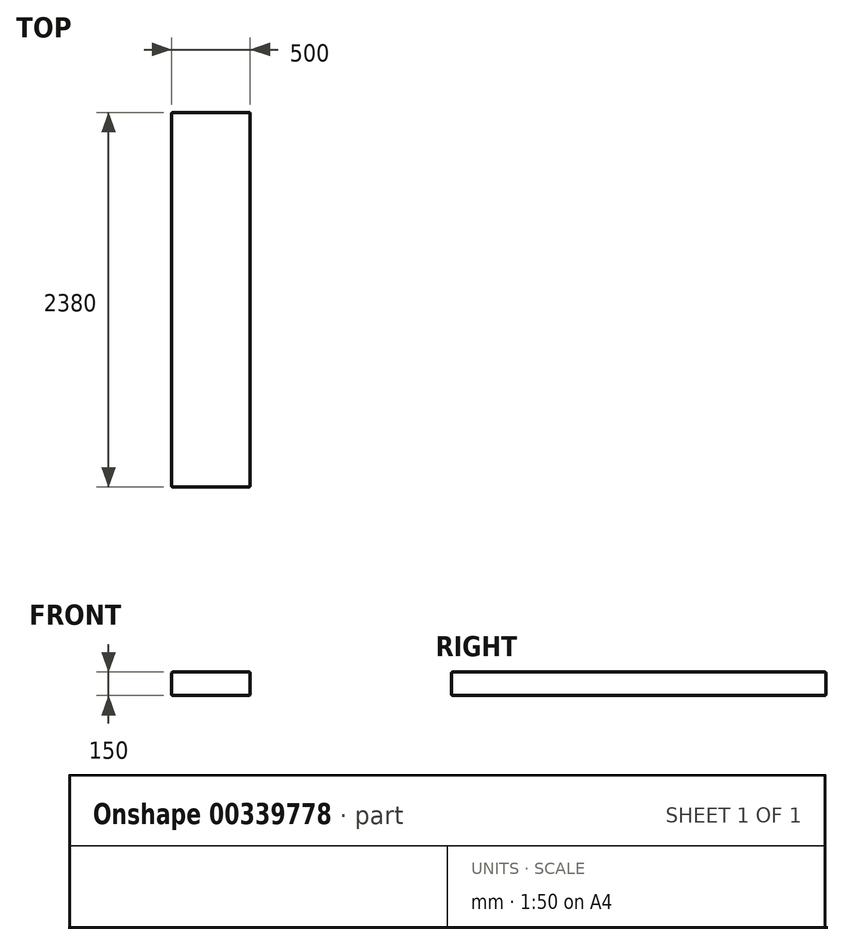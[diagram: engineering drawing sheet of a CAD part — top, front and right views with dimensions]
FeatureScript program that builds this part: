
annotation { "Feature Type Name" : "Feature", "Feature Type Description" : "" }
export const myFeature = defineFeature(function(context is Context, id is Id, definition is map)
    precondition{}
    {
        {
            var Q0;
            Q0=qCreatedBy(makeId("Top.planeOp"),FACE);
            var sketch = newSketch(context, id + "F0", { "sketchPlane" : qUnion([Q0])});
            skLineSegment(sketch, "E0.bottom", {"start": v(0, 0) * mm, "end": v(500, 0) * mm});
            skLineSegment(sketch, "E0.top", {"start": v(0, 2380) * mm, "end": v(500, 2380) * mm});
            skLineSegment(sketch, "E0.left", {"start": v(0, 0) * mm, "end": v(0, 2380) * mm});
            skLineSegment(sketch, "E0.right", {"start": v(500, 0) * mm, "end": v(500, 2380) * mm});
            skSolve(sketch);
        }
        {
            var Q0;
            Q0=makeQuery(id+"F0.imprint","IMPRINT",FACE,{"disambiguationData":[TD([[makeQuery(id+"F0.imprint","IMPRINT",EDGE,{"derivedFrom":sQuery(id+"F0.wireOp",EDGE,"E0.bottom")}),1.0]])]});
            extrude(context, id + "F1", {"entities" : qUnion([Q0]), "depth" : 150 * mm});
        }
        {
            var Q0;
            Q0=makeQuery(id+"F1.opExtrude","CAP_FACE",FACE,{"disambiguationData":[OSD([sQuery(id+"F0.wireOp",EDGE,"E0.bottom"),sQuery(id+"F0.wireOp",EDGE,"E0.top"),sQuery(id+"F0.wireOp",EDGE,"E0.left"),sQuery(id+"F0.wireOp",EDGE,"E0.right")])],"isStart":false});
            var Q1;
            Q1=makeQuery(id+"F1.opExtrude","SWEPT_FACE",FACE,{"disambiguationData":[OSD([sQuery(id+"F0.wireOp",EDGE,"E0.right")])]});
            var Q2;
            Q2=makeQuery(id+"F1.opExtrude","SWEPT_FACE",FACE,{"disambiguationData":[OSD([sQuery(id+"F0.wireOp",EDGE,"E0.bottom")])]});
            var Q3;
            Q3=makeQuery(id+"F1.opExtrude","SWEPT_FACE",FACE,{"disambiguationData":[OSD([sQuery(id+"F0.wireOp",EDGE,"E0.left")])]});
            var Q4;
            Q4=makeQuery(id+"F1.opExtrude","SWEPT_FACE",FACE,{"disambiguationData":[OSD([sQuery(id+"F0.wireOp",EDGE,"E0.top")])]});
            var Q5;
            Q5=makeQuery(id+"F1.opExtrude","CAP_FACE",FACE,{"disambiguationData":[OSD([sQuery(id+"F0.wireOp",EDGE,"E0.bottom"),sQuery(id+"F0.wireOp",EDGE,"E0.top"),sQuery(id+"F0.wireOp",EDGE,"E0.left"),sQuery(id+"F0.wireOp",EDGE,"E0.right")])],"isStart":true});
            fillet(context, id + "F2", {"entities" : qUnion([Q0, Q1, Q2, Q3, Q4, Q5]), "radius" : 10 * mm, "tangentPropagation" : true, "allowEdgeOverflow" : false});
        }
    });
